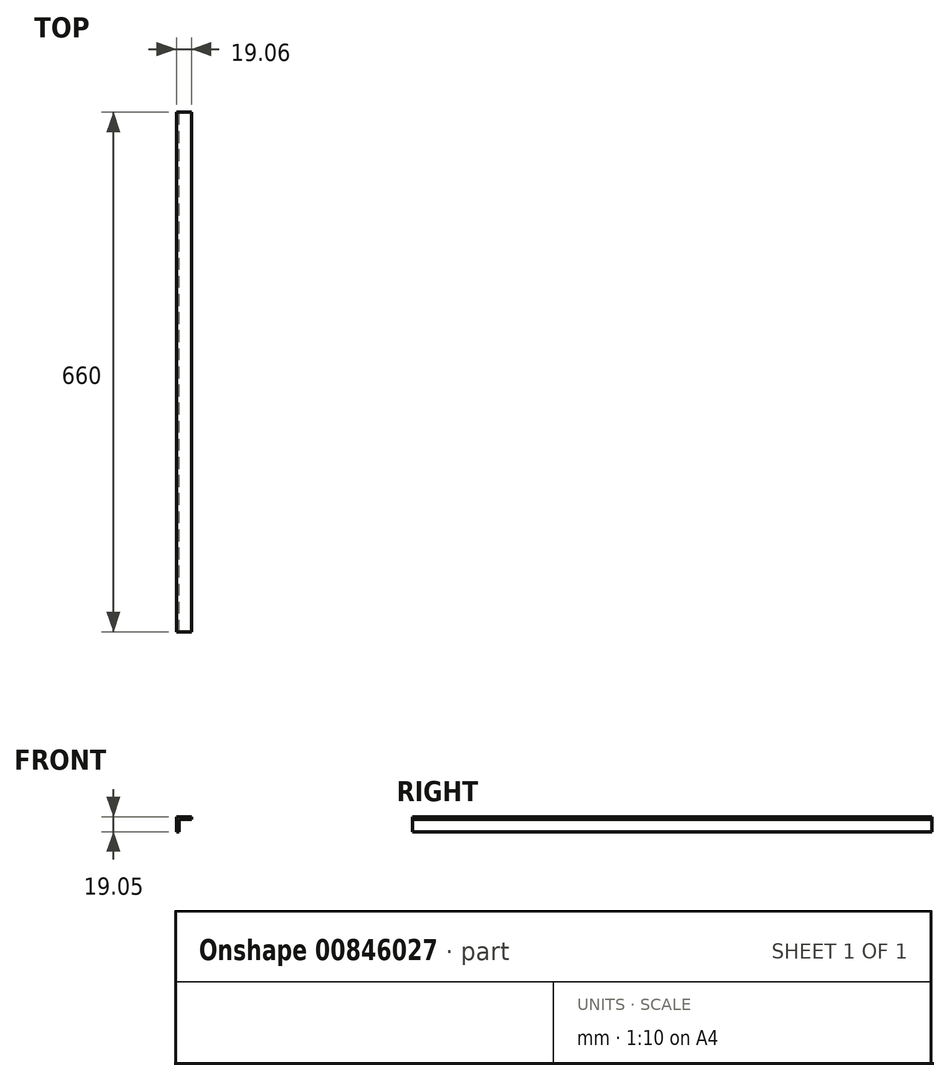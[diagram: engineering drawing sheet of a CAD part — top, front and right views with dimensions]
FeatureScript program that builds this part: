
annotation { "Feature Type Name" : "Feature", "Feature Type Description" : "" }
export const myFeature = defineFeature(function(context is Context, id is Id, definition is map)
    precondition{}
    {
        {
            var Q0;
            Q0=qCreatedBy(makeId("Front.planeOp"),FACE);
            var sketch = newSketch(context, id + "F0", { "sketchPlane" : qUnion([Q0])});
            skLineSegment(sketch, "E0", {"start": v(-9.53, 0) * mm, "end": v(-9.53, -19.05) * mm});
            skLineSegment(sketch, "E1", {"start": v(-9.53, -19.05) * mm, "end": v(-6.35, -19.05) * mm});
            skLineSegment(sketch, "E2", {"start": v(-6.35, -19.05) * mm, "end": v(-6.35, -3.17) * mm});
            skLineSegment(sketch, "E3", {"start": v(-6.35, -3.17) * mm, "end": v(9.53, -3.17) * mm});
            skLineSegment(sketch, "E4", {"start": v(9.53, -3.17) * mm, "end": v(9.53, 0) * mm});
            skLineSegment(sketch, "E5", {"start": v(9.53, 0) * mm, "end": v(-9.53, 0) * mm});
            skSolve(sketch);
        }
        {
            var Q0;
            Q0=makeQuery(id+"F0.imprint","IMPRINT",FACE,{"disambiguationData":[TD([[makeQuery(id+"F0.imprint","IMPRINT",EDGE,{"derivedFrom":sQuery(id+"F0.wireOp",EDGE,"E0")}),1.0]])]});
            extrude(context, id + "F1", {"entities" : qUnion([Q0]), "depth" : 660 * mm, "offsetDistance" : 25.4 * mm});
        }
    });
